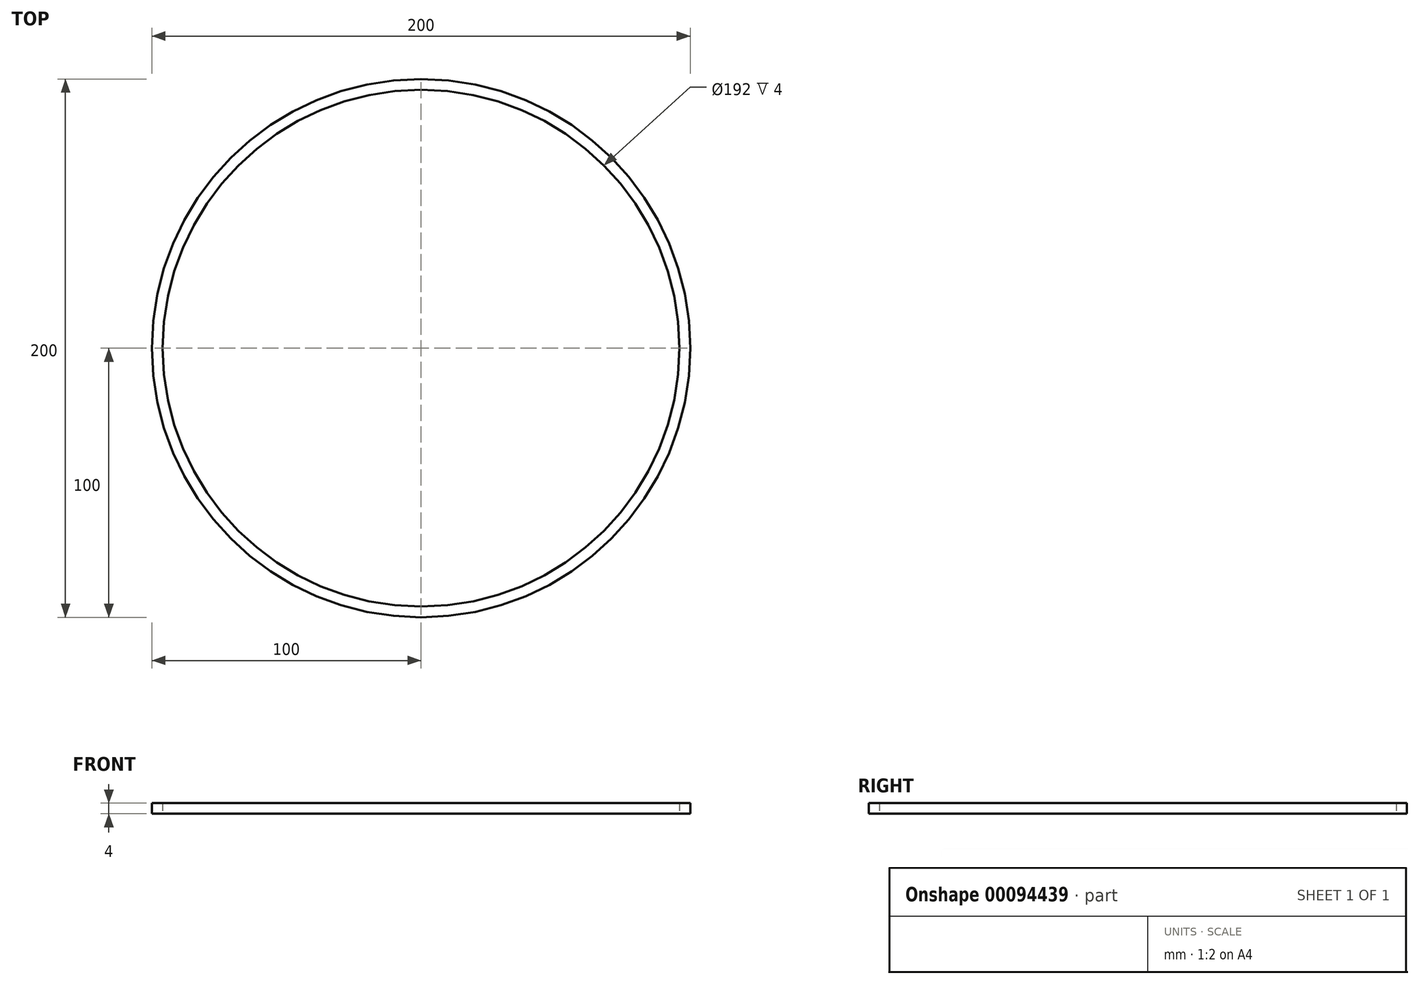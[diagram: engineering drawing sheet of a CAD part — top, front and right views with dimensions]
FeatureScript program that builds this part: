
annotation { "Feature Type Name" : "Feature", "Feature Type Description" : "" }
export const myFeature = defineFeature(function(context is Context, id is Id, definition is map)
    precondition{}
    {
        {
            var Q0;
            Q0=qCreatedBy(makeId("Top.planeOp"),FACE);
            var sketch = newSketch(context, id + "F0", { "sketchPlane" : qUnion([Q0])});
            skCircle(sketch, "E0", {"center": v(0, 0) * mm, "radius": 100 * mm});
            skCircle(sketch, "E1", {"center": v(0, 0) * mm, "radius": 96 * mm});
            skSolve(sketch);
        }
        {
            var Q0;
            Q0 = qSketchRegion(id + "F0", true);
            extrude(context, id + "F1", {"entities" : qUnion([Q0]), "depth" : 4 * mm});
        }
    });
